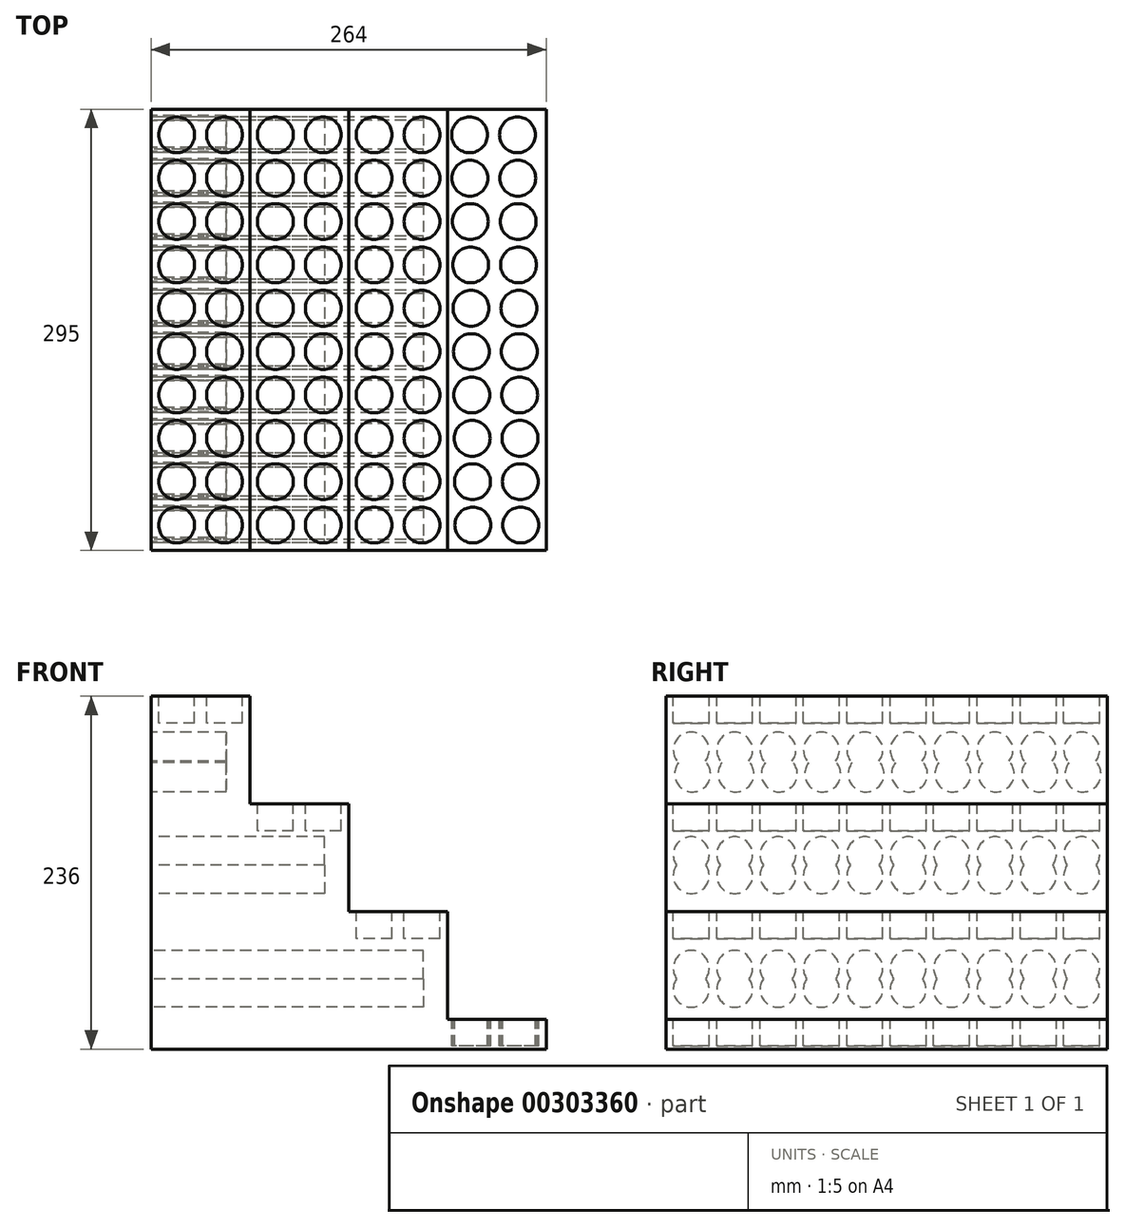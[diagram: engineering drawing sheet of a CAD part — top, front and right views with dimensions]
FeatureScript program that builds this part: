
annotation { "Feature Type Name" : "Feature", "Feature Type Description" : "" }
export const myFeature = defineFeature(function(context is Context, id is Id, definition is map)
    precondition{}
    {
        {
            var Q0;
            Q0=qCreatedBy(makeId("Front.planeOp"),FACE);
            var sketch = newSketch(context, id + "F0", { "sketchPlane" : qUnion([Q0])});
            skLineSegment(sketch, "E0", {"start": v(-130.71, -126.65) * mm, "end": v(133.29, -126.65) * mm});
            skLineSegment(sketch, "E1", {"start": v(133.29, -126.65) * mm, "end": v(133.29, -106.65) * mm});
            skLineSegment(sketch, "E2", {"start": v(133.29, -106.65) * mm, "end": v(67.29, -106.65) * mm});
            skLineSegment(sketch, "E3", {"start": v(67.29, -106.65) * mm, "end": v(67.29, -34.65) * mm});
            skLineSegment(sketch, "E4", {"start": v(67.29, -34.65) * mm, "end": v(1.29, -34.65) * mm});
            skLineSegment(sketch, "E5", {"start": v(1.29, -34.65) * mm, "end": v(1.29, 37.35) * mm});
            skLineSegment(sketch, "E6", {"start": v(1.29, 37.35) * mm, "end": v(-64.71, 37.35) * mm});
            skLineSegment(sketch, "E7", {"start": v(-64.71, 37.35) * mm, "end": v(-64.71, 109.35) * mm});
            skLineSegment(sketch, "E8", {"start": v(-64.71, 109.35) * mm, "end": v(-130.71, 109.35) * mm});
            skLineSegment(sketch, "E9", {"start": v(-130.71, 109.35) * mm, "end": v(-130.71, -126.65) * mm});
            skSolve(sketch);
        }
        {
            var Q0;
            Q0 = qSketchRegion(id + "F0", true);
            extrude(context, id + "F1", {"entities" : qUnion([Q0]), "depth" : 295 * mm});
        }
        {
            var Q0;
            Q0=makeQuery(id+"F1.opExtrude","SWEPT_FACE",FACE,{"disambiguationData":[OSD([sQuery(id+"F0.wireOp",EDGE,"E2")])]});
            var sketch = newSketch(context, id + "F2", { "sketchPlane" : qUnion([Q0])});
            skCircle(sketch, "E10", {"center": v(84.29, -278) * mm, "radius": 12 * mm});
            skCircle(sketch, "E11.0.1.0", {"center": v(84.04, -249) * mm, "radius": 12 * mm});
            skCircle(sketch, "E11.0.2.0", {"center": v(83.8, -220) * mm, "radius": 12 * mm});
            skCircle(sketch, "E11.0.3.0", {"center": v(83.55, -191) * mm, "radius": 12 * mm});
            skCircle(sketch, "E11.0.4.0", {"center": v(83.31, -162) * mm, "radius": 12 * mm});
            skCircle(sketch, "E11.0.5.0", {"center": v(83.07, -133) * mm, "radius": 12 * mm});
            skCircle(sketch, "E11.0.6.0", {"center": v(82.82, -104) * mm, "radius": 12 * mm});
            skCircle(sketch, "E11.0.7.0", {"center": v(82.58, -75) * mm, "radius": 12 * mm});
            skCircle(sketch, "E11.0.8.0", {"center": v(82.34, -46) * mm, "radius": 12 * mm});
            skCircle(sketch, "E11.0.9.0", {"center": v(82.1, -17) * mm, "radius": 12 * mm});
            skCircle(sketch, "E11.1.0.0", {"center": v(116.29, -278) * mm, "radius": 12 * mm});
            skCircle(sketch, "E11.1.1.0", {"center": v(116.04, -249) * mm, "radius": 12 * mm});
            skCircle(sketch, "E11.1.2.0", {"center": v(115.8, -220) * mm, "radius": 12 * mm});
            skCircle(sketch, "E11.1.3.0", {"center": v(115.55, -191) * mm, "radius": 12 * mm});
            skCircle(sketch, "E11.1.4.0", {"center": v(115.31, -162) * mm, "radius": 12 * mm});
            skCircle(sketch, "E11.1.5.0", {"center": v(115.07, -133) * mm, "radius": 12 * mm});
            skCircle(sketch, "E11.1.6.0", {"center": v(114.82, -104) * mm, "radius": 12 * mm});
            skCircle(sketch, "E11.1.7.0", {"center": v(114.58, -75) * mm, "radius": 12 * mm});
            skCircle(sketch, "E11.1.8.0", {"center": v(114.34, -46) * mm, "radius": 12 * mm});
            skCircle(sketch, "E11.1.9.0", {"center": v(114.1, -17) * mm, "radius": 12 * mm});
            skLineSegment(sketch, "E11.direction1", {"start": v(84.29, -278) * mm, "end": v(116.29, -278) * mm, "construction": true});
            skLineSegment(sketch, "E11.direction2", {"start": v(84.29, -278) * mm, "end": v(84.04, -249) * mm, "construction": true});
            skSolve(sketch);
        }
        {
            var Q0;
            Q0=makeQuery(id+"F2.imprint","IMPRINT",FACE,{"disambiguationData":[TD([[makeQuery(id+"F2.imprint","IMPRINT",EDGE,{"derivedFrom":sQuery(id+"F2.wireOp",EDGE,"E10")}),1.0]])]});
            var Q1;
            Q1=makeQuery(id+"F2.imprint","IMPRINT",FACE,{"disambiguationData":[TD([[makeQuery(id+"F2.imprint","IMPRINT",EDGE,{"derivedFrom":sQuery(id+"F2.wireOp",EDGE,"E11.0.1.0")}),1.0]])]});
            var Q2;
            Q2=makeQuery(id+"F2.imprint","IMPRINT",FACE,{"disambiguationData":[TD([[makeQuery(id+"F2.imprint","IMPRINT",EDGE,{"derivedFrom":sQuery(id+"F2.wireOp",EDGE,"E11.0.2.0")}),1.0]])]});
            var Q3;
            Q3=makeQuery(id+"F2.imprint","IMPRINT",FACE,{"disambiguationData":[TD([[makeQuery(id+"F2.imprint","IMPRINT",EDGE,{"derivedFrom":sQuery(id+"F2.wireOp",EDGE,"E11.0.3.0")}),1.0]])]});
            var Q4;
            Q4=makeQuery(id+"F2.imprint","IMPRINT",FACE,{"disambiguationData":[TD([[makeQuery(id+"F2.imprint","IMPRINT",EDGE,{"derivedFrom":sQuery(id+"F2.wireOp",EDGE,"E11.0.4.0")}),1.0]])]});
            var Q5;
            Q5=makeQuery(id+"F2.imprint","IMPRINT",FACE,{"disambiguationData":[TD([[makeQuery(id+"F2.imprint","IMPRINT",EDGE,{"derivedFrom":sQuery(id+"F2.wireOp",EDGE,"E11.0.5.0")}),1.0]])]});
            var Q6;
            Q6=makeQuery(id+"F2.imprint","IMPRINT",FACE,{"disambiguationData":[TD([[makeQuery(id+"F2.imprint","IMPRINT",EDGE,{"derivedFrom":sQuery(id+"F2.wireOp",EDGE,"E11.0.6.0")}),1.0]])]});
            var Q7;
            Q7=makeQuery(id+"F2.imprint","IMPRINT",FACE,{"disambiguationData":[TD([[makeQuery(id+"F2.imprint","IMPRINT",EDGE,{"derivedFrom":sQuery(id+"F2.wireOp",EDGE,"E11.0.7.0")}),1.0]])]});
            var Q8;
            Q8=makeQuery(id+"F2.imprint","IMPRINT",FACE,{"disambiguationData":[TD([[makeQuery(id+"F2.imprint","IMPRINT",EDGE,{"derivedFrom":sQuery(id+"F2.wireOp",EDGE,"E11.0.8.0")}),1.0]])]});
            var Q9;
            Q9=makeQuery(id+"F2.imprint","IMPRINT",FACE,{"disambiguationData":[TD([[makeQuery(id+"F2.imprint","IMPRINT",EDGE,{"derivedFrom":sQuery(id+"F2.wireOp",EDGE,"E11.0.9.0")}),1.0]])]});
            var Q10;
            Q10=makeQuery(id+"F2.imprint","IMPRINT",FACE,{"disambiguationData":[TD([[makeQuery(id+"F2.imprint","IMPRINT",EDGE,{"derivedFrom":sQuery(id+"F2.wireOp",EDGE,"E11.1.9.0")}),1.0]])]});
            var Q11;
            Q11=makeQuery(id+"F2.imprint","IMPRINT",FACE,{"disambiguationData":[TD([[makeQuery(id+"F2.imprint","IMPRINT",EDGE,{"derivedFrom":sQuery(id+"F2.wireOp",EDGE,"E11.1.8.0")}),1.0]])]});
            var Q12;
            Q12=makeQuery(id+"F2.imprint","IMPRINT",FACE,{"disambiguationData":[TD([[makeQuery(id+"F2.imprint","IMPRINT",EDGE,{"derivedFrom":sQuery(id+"F2.wireOp",EDGE,"E11.1.7.0")}),1.0]])]});
            var Q13;
            Q13=makeQuery(id+"F2.imprint","IMPRINT",FACE,{"disambiguationData":[TD([[makeQuery(id+"F2.imprint","IMPRINT",EDGE,{"derivedFrom":sQuery(id+"F2.wireOp",EDGE,"E11.1.6.0")}),1.0]])]});
            var Q14;
            Q14=makeQuery(id+"F2.imprint","IMPRINT",FACE,{"disambiguationData":[TD([[makeQuery(id+"F2.imprint","IMPRINT",EDGE,{"derivedFrom":sQuery(id+"F2.wireOp",EDGE,"E11.1.5.0")}),1.0]])]});
            var Q15;
            Q15=makeQuery(id+"F2.imprint","IMPRINT",FACE,{"disambiguationData":[TD([[makeQuery(id+"F2.imprint","IMPRINT",EDGE,{"derivedFrom":sQuery(id+"F2.wireOp",EDGE,"E11.1.4.0")}),1.0]])]});
            var Q16;
            Q16=makeQuery(id+"F2.imprint","IMPRINT",FACE,{"disambiguationData":[TD([[makeQuery(id+"F2.imprint","IMPRINT",EDGE,{"derivedFrom":sQuery(id+"F2.wireOp",EDGE,"E11.1.3.0")}),1.0]])]});
            var Q17;
            Q17=makeQuery(id+"F2.imprint","IMPRINT",FACE,{"disambiguationData":[TD([[makeQuery(id+"F2.imprint","IMPRINT",EDGE,{"derivedFrom":sQuery(id+"F2.wireOp",EDGE,"E11.1.2.0")}),1.0]])]});
            var Q18;
            Q18=makeQuery(id+"F2.imprint","IMPRINT",FACE,{"disambiguationData":[TD([[makeQuery(id+"F2.imprint","IMPRINT",EDGE,{"derivedFrom":sQuery(id+"F2.wireOp",EDGE,"E11.1.1.0")}),1.0]])]});
            var Q19;
            Q19=makeQuery(id+"F2.imprint","IMPRINT",FACE,{"disambiguationData":[TD([[makeQuery(id+"F2.imprint","IMPRINT",EDGE,{"derivedFrom":sQuery(id+"F2.wireOp",EDGE,"E11.1.0.0")}),1.0]])]});
            var Q20;
            Q20=sQuery(id+"F2.wireOp",EDGE,"E10");
            extrude(context, id + "F3", {"entities" : qUnion([Q0, Q1, Q2, Q3, Q4, Q5, Q6, Q7, Q8, Q9, Q10, Q11, Q12, Q13, Q14, Q15, Q16, Q17, Q18, Q19]), "operationType" : NewBodyOperationType.REMOVE, "surfaceEntities" : qUnion([Q20]), "oppositeDirection" : true, "depth" : 18 * mm});
        }
        {
            var Q0;
            Q0=makeQuery(id+"F1.opExtrude","SWEPT_FACE",FACE,{"disambiguationData":[OSD([sQuery(id+"F0.wireOp",EDGE,"E4")])]});
            var sketch = newSketch(context, id + "F4", { "sketchPlane" : qUnion([Q0])});
            skCircle(sketch, "E12", {"center": v(18.29, -278) * mm, "radius": 12 * mm});
            skCircle(sketch, "E13.0.1.0", {"center": v(18.29, -249) * mm, "radius": 12 * mm});
            skCircle(sketch, "E13.0.2.0", {"center": v(18.29, -220) * mm, "radius": 12 * mm});
            skCircle(sketch, "E13.0.3.0", {"center": v(18.29, -191) * mm, "radius": 12 * mm});
            skCircle(sketch, "E13.0.4.0", {"center": v(18.29, -162) * mm, "radius": 12 * mm});
            skCircle(sketch, "E13.0.5.0", {"center": v(18.29, -133) * mm, "radius": 12 * mm});
            skCircle(sketch, "E13.0.6.0", {"center": v(18.29, -104) * mm, "radius": 12 * mm});
            skCircle(sketch, "E13.0.7.0", {"center": v(18.29, -75) * mm, "radius": 12 * mm});
            skCircle(sketch, "E13.0.8.0", {"center": v(18.29, -46) * mm, "radius": 12 * mm});
            skCircle(sketch, "E13.0.9.0", {"center": v(18.29, -17) * mm, "radius": 12 * mm});
            skCircle(sketch, "E13.1.0.0", {"center": v(50.29, -278) * mm, "radius": 12 * mm});
            skCircle(sketch, "E13.1.1.0", {"center": v(50.29, -249) * mm, "radius": 12 * mm});
            skCircle(sketch, "E13.1.2.0", {"center": v(50.29, -220) * mm, "radius": 12 * mm});
            skCircle(sketch, "E13.1.3.0", {"center": v(50.29, -191) * mm, "radius": 12 * mm});
            skCircle(sketch, "E13.1.4.0", {"center": v(50.29, -162) * mm, "radius": 12 * mm});
            skCircle(sketch, "E13.1.5.0", {"center": v(50.29, -133) * mm, "radius": 12 * mm});
            skCircle(sketch, "E13.1.6.0", {"center": v(50.29, -104) * mm, "radius": 12 * mm});
            skCircle(sketch, "E13.1.7.0", {"center": v(50.29, -75) * mm, "radius": 12 * mm});
            skCircle(sketch, "E13.1.8.0", {"center": v(50.29, -46) * mm, "radius": 12 * mm});
            skCircle(sketch, "E13.1.9.0", {"center": v(50.29, -17) * mm, "radius": 12 * mm});
            skLineSegment(sketch, "E13.direction1", {"start": v(18.29, -278) * mm, "end": v(50.29, -278) * mm, "construction": true});
            skLineSegment(sketch, "E13.direction2", {"start": v(18.29, -278) * mm, "end": v(18.29, -249) * mm, "construction": true});
            skSolve(sketch);
        }
        {
            var Q0;
            Q0=makeQuery(id+"F4.imprint","IMPRINT",FACE,{"disambiguationData":[TD([[makeQuery(id+"F4.imprint","IMPRINT",EDGE,{"derivedFrom":sQuery(id+"F4.wireOp",EDGE,"E12")}),1.0]])]});
            var Q1;
            Q1=makeQuery(id+"F4.imprint","IMPRINT",FACE,{"disambiguationData":[TD([[makeQuery(id+"F4.imprint","IMPRINT",EDGE,{"derivedFrom":sQuery(id+"F4.wireOp",EDGE,"E13.0.1.0")}),1.0]])]});
            var Q2;
            Q2=makeQuery(id+"F4.imprint","IMPRINT",FACE,{"disambiguationData":[TD([[makeQuery(id+"F4.imprint","IMPRINT",EDGE,{"derivedFrom":sQuery(id+"F4.wireOp",EDGE,"E13.0.2.0")}),1.0]])]});
            var Q3;
            Q3=makeQuery(id+"F4.imprint","IMPRINT",FACE,{"disambiguationData":[TD([[makeQuery(id+"F4.imprint","IMPRINT",EDGE,{"derivedFrom":sQuery(id+"F4.wireOp",EDGE,"E13.0.3.0")}),1.0]])]});
            var Q4;
            Q4=makeQuery(id+"F4.imprint","IMPRINT",FACE,{"disambiguationData":[TD([[makeQuery(id+"F4.imprint","IMPRINT",EDGE,{"derivedFrom":sQuery(id+"F4.wireOp",EDGE,"E13.0.4.0")}),1.0]])]});
            var Q5;
            Q5=makeQuery(id+"F4.imprint","IMPRINT",FACE,{"disambiguationData":[TD([[makeQuery(id+"F4.imprint","IMPRINT",EDGE,{"derivedFrom":sQuery(id+"F4.wireOp",EDGE,"E13.0.5.0")}),1.0]])]});
            var Q6;
            Q6=makeQuery(id+"F4.imprint","IMPRINT",FACE,{"disambiguationData":[TD([[makeQuery(id+"F4.imprint","IMPRINT",EDGE,{"derivedFrom":sQuery(id+"F4.wireOp",EDGE,"E13.0.6.0")}),1.0]])]});
            var Q7;
            Q7=makeQuery(id+"F4.imprint","IMPRINT",FACE,{"disambiguationData":[TD([[makeQuery(id+"F4.imprint","IMPRINT",EDGE,{"derivedFrom":sQuery(id+"F4.wireOp",EDGE,"E13.0.7.0")}),1.0]])]});
            var Q8;
            Q8=makeQuery(id+"F4.imprint","IMPRINT",FACE,{"disambiguationData":[TD([[makeQuery(id+"F4.imprint","IMPRINT",EDGE,{"derivedFrom":sQuery(id+"F4.wireOp",EDGE,"E13.0.8.0")}),1.0]])]});
            var Q9;
            Q9=makeQuery(id+"F4.imprint","IMPRINT",FACE,{"disambiguationData":[TD([[makeQuery(id+"F4.imprint","IMPRINT",EDGE,{"derivedFrom":sQuery(id+"F4.wireOp",EDGE,"E13.0.9.0")}),1.0]])]});
            var Q10;
            Q10=makeQuery(id+"F4.imprint","IMPRINT",FACE,{"disambiguationData":[TD([[makeQuery(id+"F4.imprint","IMPRINT",EDGE,{"derivedFrom":sQuery(id+"F4.wireOp",EDGE,"E13.1.9.0")}),1.0]])]});
            var Q11;
            Q11=makeQuery(id+"F4.imprint","IMPRINT",FACE,{"disambiguationData":[TD([[makeQuery(id+"F4.imprint","IMPRINT",EDGE,{"derivedFrom":sQuery(id+"F4.wireOp",EDGE,"E13.1.8.0")}),1.0]])]});
            var Q12;
            Q12=makeQuery(id+"F4.imprint","IMPRINT",FACE,{"disambiguationData":[TD([[makeQuery(id+"F4.imprint","IMPRINT",EDGE,{"derivedFrom":sQuery(id+"F4.wireOp",EDGE,"E13.1.7.0")}),1.0]])]});
            var Q13;
            Q13=makeQuery(id+"F4.imprint","IMPRINT",FACE,{"disambiguationData":[TD([[makeQuery(id+"F4.imprint","IMPRINT",EDGE,{"derivedFrom":sQuery(id+"F4.wireOp",EDGE,"E13.1.6.0")}),1.0]])]});
            var Q14;
            Q14=makeQuery(id+"F4.imprint","IMPRINT",FACE,{"disambiguationData":[TD([[makeQuery(id+"F4.imprint","IMPRINT",EDGE,{"derivedFrom":sQuery(id+"F4.wireOp",EDGE,"E13.1.5.0")}),1.0]])]});
            var Q15;
            Q15=makeQuery(id+"F4.imprint","IMPRINT",FACE,{"disambiguationData":[TD([[makeQuery(id+"F4.imprint","IMPRINT",EDGE,{"derivedFrom":sQuery(id+"F4.wireOp",EDGE,"E13.1.4.0")}),1.0]])]});
            var Q16;
            Q16=makeQuery(id+"F4.imprint","IMPRINT",FACE,{"disambiguationData":[TD([[makeQuery(id+"F4.imprint","IMPRINT",EDGE,{"derivedFrom":sQuery(id+"F4.wireOp",EDGE,"E13.1.3.0")}),1.0]])]});
            var Q17;
            Q17=makeQuery(id+"F4.imprint","IMPRINT",FACE,{"disambiguationData":[TD([[makeQuery(id+"F4.imprint","IMPRINT",EDGE,{"derivedFrom":sQuery(id+"F4.wireOp",EDGE,"E13.1.2.0")}),1.0]])]});
            var Q18;
            Q18=makeQuery(id+"F4.imprint","IMPRINT",FACE,{"disambiguationData":[TD([[makeQuery(id+"F4.imprint","IMPRINT",EDGE,{"derivedFrom":sQuery(id+"F4.wireOp",EDGE,"E13.1.1.0")}),1.0]])]});
            var Q19;
            Q19=makeQuery(id+"F4.imprint","IMPRINT",FACE,{"disambiguationData":[TD([[makeQuery(id+"F4.imprint","IMPRINT",EDGE,{"derivedFrom":sQuery(id+"F4.wireOp",EDGE,"E13.1.0.0")}),1.0]])]});
            var Q20;
            Q20=sQuery(id+"F4.wireOp",EDGE,"E12");
            extrude(context, id + "F5", {"entities" : qUnion([Q0, Q1, Q2, Q3, Q4, Q5, Q6, Q7, Q8, Q9, Q10, Q11, Q12, Q13, Q14, Q15, Q16, Q17, Q18, Q19]), "operationType" : NewBodyOperationType.REMOVE, "surfaceEntities" : qUnion([Q20]), "oppositeDirection" : true, "depth" : 18 * mm});
        }
        {
            var Q0;
            Q0=makeQuery(id+"F1.opExtrude","SWEPT_FACE",FACE,{"disambiguationData":[OSD([sQuery(id+"F0.wireOp",EDGE,"E6")])]});
            var sketch = newSketch(context, id + "F6", { "sketchPlane" : qUnion([Q0])});
            skCircle(sketch, "E14", {"center": v(-47.71, -278) * mm, "radius": 12 * mm});
            skCircle(sketch, "E15.0.1.0", {"center": v(-47.71, -249) * mm, "radius": 12 * mm});
            skCircle(sketch, "E15.0.2.0", {"center": v(-47.71, -220) * mm, "radius": 12 * mm});
            skCircle(sketch, "E15.0.3.0", {"center": v(-47.71, -191) * mm, "radius": 12 * mm});
            skCircle(sketch, "E15.0.4.0", {"center": v(-47.71, -162) * mm, "radius": 12 * mm});
            skCircle(sketch, "E15.0.5.0", {"center": v(-47.71, -133) * mm, "radius": 12 * mm});
            skCircle(sketch, "E15.0.6.0", {"center": v(-47.71, -104) * mm, "radius": 12 * mm});
            skCircle(sketch, "E15.0.7.0", {"center": v(-47.71, -75) * mm, "radius": 12 * mm});
            skCircle(sketch, "E15.0.8.0", {"center": v(-47.71, -46) * mm, "radius": 12 * mm});
            skCircle(sketch, "E15.0.9.0", {"center": v(-47.71, -17) * mm, "radius": 12 * mm});
            skCircle(sketch, "E15.1.0.0", {"center": v(-15.71, -278) * mm, "radius": 12 * mm});
            skCircle(sketch, "E15.1.1.0", {"center": v(-15.71, -249) * mm, "radius": 12 * mm});
            skCircle(sketch, "E15.1.2.0", {"center": v(-15.71, -220) * mm, "radius": 12 * mm});
            skCircle(sketch, "E15.1.3.0", {"center": v(-15.71, -191) * mm, "radius": 12 * mm});
            skCircle(sketch, "E15.1.4.0", {"center": v(-15.71, -162) * mm, "radius": 12 * mm});
            skCircle(sketch, "E15.1.5.0", {"center": v(-15.71, -133) * mm, "radius": 12 * mm});
            skCircle(sketch, "E15.1.6.0", {"center": v(-15.71, -104) * mm, "radius": 12 * mm});
            skCircle(sketch, "E15.1.7.0", {"center": v(-15.71, -75) * mm, "radius": 12 * mm});
            skCircle(sketch, "E15.1.8.0", {"center": v(-15.71, -46) * mm, "radius": 12 * mm});
            skCircle(sketch, "E15.1.9.0", {"center": v(-15.71, -17) * mm, "radius": 12 * mm});
            skLineSegment(sketch, "E15.direction1", {"start": v(-47.71, -278) * mm, "end": v(-15.71, -278) * mm, "construction": true});
            skLineSegment(sketch, "E15.direction2", {"start": v(-47.71, -278) * mm, "end": v(-47.71, -249) * mm, "construction": true});
            skSolve(sketch);
        }
        {
            var Q0;
            Q0=makeQuery(id+"F6.imprint","IMPRINT",FACE,{"disambiguationData":[TD([[makeQuery(id+"F6.imprint","IMPRINT",EDGE,{"derivedFrom":sQuery(id+"F6.wireOp",EDGE,"E14")}),1.0]])]});
            var Q1;
            Q1=makeQuery(id+"F6.imprint","IMPRINT",FACE,{"disambiguationData":[TD([[makeQuery(id+"F6.imprint","IMPRINT",EDGE,{"derivedFrom":sQuery(id+"F6.wireOp",EDGE,"E15.0.1.0")}),1.0]])]});
            var Q2;
            Q2=makeQuery(id+"F6.imprint","IMPRINT",FACE,{"disambiguationData":[TD([[makeQuery(id+"F6.imprint","IMPRINT",EDGE,{"derivedFrom":sQuery(id+"F6.wireOp",EDGE,"E15.0.2.0")}),1.0]])]});
            var Q3;
            Q3=makeQuery(id+"F6.imprint","IMPRINT",FACE,{"disambiguationData":[TD([[makeQuery(id+"F6.imprint","IMPRINT",EDGE,{"derivedFrom":sQuery(id+"F6.wireOp",EDGE,"E15.0.3.0")}),1.0]])]});
            var Q4;
            Q4=makeQuery(id+"F6.imprint","IMPRINT",FACE,{"disambiguationData":[TD([[makeQuery(id+"F6.imprint","IMPRINT",EDGE,{"derivedFrom":sQuery(id+"F6.wireOp",EDGE,"E15.0.4.0")}),1.0]])]});
            var Q5;
            Q5=makeQuery(id+"F6.imprint","IMPRINT",FACE,{"disambiguationData":[TD([[makeQuery(id+"F6.imprint","IMPRINT",EDGE,{"derivedFrom":sQuery(id+"F6.wireOp",EDGE,"E15.0.5.0")}),1.0]])]});
            var Q6;
            Q6=makeQuery(id+"F6.imprint","IMPRINT",FACE,{"disambiguationData":[TD([[makeQuery(id+"F6.imprint","IMPRINT",EDGE,{"derivedFrom":sQuery(id+"F6.wireOp",EDGE,"E15.0.6.0")}),1.0]])]});
            var Q7;
            Q7=makeQuery(id+"F6.imprint","IMPRINT",FACE,{"disambiguationData":[TD([[makeQuery(id+"F6.imprint","IMPRINT",EDGE,{"derivedFrom":sQuery(id+"F6.wireOp",EDGE,"E15.0.7.0")}),1.0]])]});
            var Q8;
            Q8=makeQuery(id+"F6.imprint","IMPRINT",FACE,{"disambiguationData":[TD([[makeQuery(id+"F6.imprint","IMPRINT",EDGE,{"derivedFrom":sQuery(id+"F6.wireOp",EDGE,"E15.0.8.0")}),1.0]])]});
            var Q9;
            Q9=makeQuery(id+"F6.imprint","IMPRINT",FACE,{"disambiguationData":[TD([[makeQuery(id+"F6.imprint","IMPRINT",EDGE,{"derivedFrom":sQuery(id+"F6.wireOp",EDGE,"E15.0.9.0")}),1.0]])]});
            var Q10;
            Q10=makeQuery(id+"F6.imprint","IMPRINT",FACE,{"disambiguationData":[TD([[makeQuery(id+"F6.imprint","IMPRINT",EDGE,{"derivedFrom":sQuery(id+"F6.wireOp",EDGE,"E15.1.9.0")}),1.0]])]});
            var Q11;
            Q11=makeQuery(id+"F6.imprint","IMPRINT",FACE,{"disambiguationData":[TD([[makeQuery(id+"F6.imprint","IMPRINT",EDGE,{"derivedFrom":sQuery(id+"F6.wireOp",EDGE,"E15.1.8.0")}),1.0]])]});
            var Q12;
            Q12=makeQuery(id+"F6.imprint","IMPRINT",FACE,{"disambiguationData":[TD([[makeQuery(id+"F6.imprint","IMPRINT",EDGE,{"derivedFrom":sQuery(id+"F6.wireOp",EDGE,"E15.1.7.0")}),1.0]])]});
            var Q13;
            Q13=makeQuery(id+"F6.imprint","IMPRINT",FACE,{"disambiguationData":[TD([[makeQuery(id+"F6.imprint","IMPRINT",EDGE,{"derivedFrom":sQuery(id+"F6.wireOp",EDGE,"E15.1.6.0")}),1.0]])]});
            var Q14;
            Q14=makeQuery(id+"F6.imprint","IMPRINT",FACE,{"disambiguationData":[TD([[makeQuery(id+"F6.imprint","IMPRINT",EDGE,{"derivedFrom":sQuery(id+"F6.wireOp",EDGE,"E15.1.5.0")}),1.0]])]});
            var Q15;
            Q15=makeQuery(id+"F6.imprint","IMPRINT",FACE,{"disambiguationData":[TD([[makeQuery(id+"F6.imprint","IMPRINT",EDGE,{"derivedFrom":sQuery(id+"F6.wireOp",EDGE,"E15.1.4.0")}),1.0]])]});
            var Q16;
            Q16=makeQuery(id+"F6.imprint","IMPRINT",FACE,{"disambiguationData":[TD([[makeQuery(id+"F6.imprint","IMPRINT",EDGE,{"derivedFrom":sQuery(id+"F6.wireOp",EDGE,"E15.1.3.0")}),1.0]])]});
            var Q17;
            Q17=makeQuery(id+"F6.imprint","IMPRINT",FACE,{"disambiguationData":[TD([[makeQuery(id+"F6.imprint","IMPRINT",EDGE,{"derivedFrom":sQuery(id+"F6.wireOp",EDGE,"E15.1.2.0")}),1.0]])]});
            var Q18;
            Q18=makeQuery(id+"F6.imprint","IMPRINT",FACE,{"disambiguationData":[TD([[makeQuery(id+"F6.imprint","IMPRINT",EDGE,{"derivedFrom":sQuery(id+"F6.wireOp",EDGE,"E15.1.1.0")}),1.0]])]});
            var Q19;
            Q19=makeQuery(id+"F6.imprint","IMPRINT",FACE,{"disambiguationData":[TD([[makeQuery(id+"F6.imprint","IMPRINT",EDGE,{"derivedFrom":sQuery(id+"F6.wireOp",EDGE,"E15.1.0.0")}),1.0]])]});
            var Q20;
            Q20=makeQuery(id+"F6.imprint","IMPRINT",EDGE,{"derivedFrom":sQuery(id+"F6.wireOp",EDGE,"E14")});
            extrude(context, id + "F7", {"entities" : qUnion([Q0, Q1, Q2, Q3, Q4, Q5, Q6, Q7, Q8, Q9, Q10, Q11, Q12, Q13, Q14, Q15, Q16, Q17, Q18, Q19]), "operationType" : NewBodyOperationType.REMOVE, "surfaceEntities" : qUnion([Q20]), "oppositeDirection" : true, "depth" : 18 * mm});
        }
        {
            var Q0;
            Q0=makeQuery(id+"F1.opExtrude","SWEPT_FACE",FACE,{"disambiguationData":[OSD([sQuery(id+"F0.wireOp",EDGE,"E8")])]});
            var sketch = newSketch(context, id + "F8", { "sketchPlane" : qUnion([Q0])});
            skCircle(sketch, "E16", {"center": v(-113.71, -278) * mm, "radius": 12 * mm});
            skCircle(sketch, "E17.0.1.0", {"center": v(-113.71, -249) * mm, "radius": 12 * mm});
            skCircle(sketch, "E17.0.2.0", {"center": v(-113.71, -220) * mm, "radius": 12 * mm});
            skCircle(sketch, "E17.0.3.0", {"center": v(-113.71, -191) * mm, "radius": 12 * mm});
            skCircle(sketch, "E17.0.4.0", {"center": v(-113.71, -162) * mm, "radius": 12 * mm});
            skCircle(sketch, "E17.0.5.0", {"center": v(-113.71, -133) * mm, "radius": 12 * mm});
            skCircle(sketch, "E17.0.6.0", {"center": v(-113.71, -104) * mm, "radius": 12 * mm});
            skCircle(sketch, "E17.0.7.0", {"center": v(-113.71, -75) * mm, "radius": 12 * mm});
            skCircle(sketch, "E17.0.8.0", {"center": v(-113.71, -46) * mm, "radius": 12 * mm});
            skCircle(sketch, "E17.0.9.0", {"center": v(-113.71, -17) * mm, "radius": 12 * mm});
            skCircle(sketch, "E17.1.0.0", {"center": v(-81.71, -278) * mm, "radius": 12 * mm});
            skCircle(sketch, "E17.1.1.0", {"center": v(-81.71, -249) * mm, "radius": 12 * mm});
            skCircle(sketch, "E17.1.2.0", {"center": v(-81.71, -220) * mm, "radius": 12 * mm});
            skCircle(sketch, "E17.1.3.0", {"center": v(-81.71, -191) * mm, "radius": 12 * mm});
            skCircle(sketch, "E17.1.4.0", {"center": v(-81.71, -162) * mm, "radius": 12 * mm});
            skCircle(sketch, "E17.1.5.0", {"center": v(-81.71, -133) * mm, "radius": 12 * mm});
            skCircle(sketch, "E17.1.6.0", {"center": v(-81.71, -104) * mm, "radius": 12 * mm});
            skCircle(sketch, "E17.1.7.0", {"center": v(-81.71, -75) * mm, "radius": 12 * mm});
            skCircle(sketch, "E17.1.8.0", {"center": v(-81.71, -46) * mm, "radius": 12 * mm});
            skCircle(sketch, "E17.1.9.0", {"center": v(-81.71, -17) * mm, "radius": 12 * mm});
            skLineSegment(sketch, "E17.direction1", {"start": v(-113.71, -278) * mm, "end": v(-81.71, -278) * mm, "construction": true});
            skLineSegment(sketch, "E17.direction2", {"start": v(-113.71, -278) * mm, "end": v(-113.71, -249) * mm, "construction": true});
            skSolve(sketch);
        }
        {
            var Q0;
            Q0=makeQuery(id+"F8.imprint","IMPRINT",FACE,{"disambiguationData":[TD([[makeQuery(id+"F8.imprint","IMPRINT",EDGE,{"derivedFrom":sQuery(id+"F8.wireOp",EDGE,"E16")}),1.0]])]});
            var Q1;
            Q1=makeQuery(id+"F8.imprint","IMPRINT",FACE,{"disambiguationData":[TD([[makeQuery(id+"F8.imprint","IMPRINT",EDGE,{"derivedFrom":sQuery(id+"F8.wireOp",EDGE,"E17.0.1.0")}),1.0]])]});
            var Q2;
            Q2=makeQuery(id+"F8.imprint","IMPRINT",FACE,{"disambiguationData":[TD([[makeQuery(id+"F8.imprint","IMPRINT",EDGE,{"derivedFrom":sQuery(id+"F8.wireOp",EDGE,"E17.0.2.0")}),1.0]])]});
            var Q3;
            Q3=makeQuery(id+"F8.imprint","IMPRINT",FACE,{"disambiguationData":[TD([[makeQuery(id+"F8.imprint","IMPRINT",EDGE,{"derivedFrom":sQuery(id+"F8.wireOp",EDGE,"E17.0.3.0")}),1.0]])]});
            var Q4;
            Q4=makeQuery(id+"F8.imprint","IMPRINT",FACE,{"disambiguationData":[TD([[makeQuery(id+"F8.imprint","IMPRINT",EDGE,{"derivedFrom":sQuery(id+"F8.wireOp",EDGE,"E17.0.4.0")}),1.0]])]});
            var Q5;
            Q5=makeQuery(id+"F8.imprint","IMPRINT",FACE,{"disambiguationData":[TD([[makeQuery(id+"F8.imprint","IMPRINT",EDGE,{"derivedFrom":sQuery(id+"F8.wireOp",EDGE,"E17.0.5.0")}),1.0]])]});
            var Q6;
            Q6=makeQuery(id+"F8.imprint","IMPRINT",FACE,{"disambiguationData":[TD([[makeQuery(id+"F8.imprint","IMPRINT",EDGE,{"derivedFrom":sQuery(id+"F8.wireOp",EDGE,"E17.0.6.0")}),1.0]])]});
            var Q7;
            Q7=makeQuery(id+"F8.imprint","IMPRINT",FACE,{"disambiguationData":[TD([[makeQuery(id+"F8.imprint","IMPRINT",EDGE,{"derivedFrom":sQuery(id+"F8.wireOp",EDGE,"E17.0.7.0")}),1.0]])]});
            var Q8;
            Q8=makeQuery(id+"F8.imprint","IMPRINT",FACE,{"disambiguationData":[TD([[makeQuery(id+"F8.imprint","IMPRINT",EDGE,{"derivedFrom":sQuery(id+"F8.wireOp",EDGE,"E17.0.8.0")}),1.0]])]});
            var Q9;
            Q9=makeQuery(id+"F8.imprint","IMPRINT",FACE,{"disambiguationData":[TD([[makeQuery(id+"F8.imprint","IMPRINT",EDGE,{"derivedFrom":sQuery(id+"F8.wireOp",EDGE,"E17.0.9.0")}),1.0]])]});
            var Q10;
            Q10=makeQuery(id+"F8.imprint","IMPRINT",FACE,{"disambiguationData":[TD([[makeQuery(id+"F8.imprint","IMPRINT",EDGE,{"derivedFrom":sQuery(id+"F8.wireOp",EDGE,"E17.1.9.0")}),1.0]])]});
            var Q11;
            Q11=makeQuery(id+"F8.imprint","IMPRINT",FACE,{"disambiguationData":[TD([[makeQuery(id+"F8.imprint","IMPRINT",EDGE,{"derivedFrom":sQuery(id+"F8.wireOp",EDGE,"E17.1.8.0")}),1.0]])]});
            var Q12;
            Q12=makeQuery(id+"F8.imprint","IMPRINT",FACE,{"disambiguationData":[TD([[makeQuery(id+"F8.imprint","IMPRINT",EDGE,{"derivedFrom":sQuery(id+"F8.wireOp",EDGE,"E17.1.7.0")}),1.0]])]});
            var Q13;
            Q13=makeQuery(id+"F8.imprint","IMPRINT",FACE,{"disambiguationData":[TD([[makeQuery(id+"F8.imprint","IMPRINT",EDGE,{"derivedFrom":sQuery(id+"F8.wireOp",EDGE,"E17.1.6.0")}),1.0]])]});
            var Q14;
            Q14=makeQuery(id+"F8.imprint","IMPRINT",FACE,{"disambiguationData":[TD([[makeQuery(id+"F8.imprint","IMPRINT",EDGE,{"derivedFrom":sQuery(id+"F8.wireOp",EDGE,"E17.1.5.0")}),1.0]])]});
            var Q15;
            Q15=makeQuery(id+"F8.imprint","IMPRINT",FACE,{"disambiguationData":[TD([[makeQuery(id+"F8.imprint","IMPRINT",EDGE,{"derivedFrom":sQuery(id+"F8.wireOp",EDGE,"E17.1.4.0")}),1.0]])]});
            var Q16;
            Q16=makeQuery(id+"F8.imprint","IMPRINT",FACE,{"disambiguationData":[TD([[makeQuery(id+"F8.imprint","IMPRINT",EDGE,{"derivedFrom":sQuery(id+"F8.wireOp",EDGE,"E17.1.3.0")}),1.0]])]});
            var Q17;
            Q17=makeQuery(id+"F8.imprint","IMPRINT",FACE,{"disambiguationData":[TD([[makeQuery(id+"F8.imprint","IMPRINT",EDGE,{"derivedFrom":sQuery(id+"F8.wireOp",EDGE,"E17.1.2.0")}),1.0]])]});
            var Q18;
            Q18=makeQuery(id+"F8.imprint","IMPRINT",FACE,{"disambiguationData":[TD([[makeQuery(id+"F8.imprint","IMPRINT",EDGE,{"derivedFrom":sQuery(id+"F8.wireOp",EDGE,"E17.1.1.0")}),1.0]])]});
            var Q19;
            Q19=makeQuery(id+"F8.imprint","IMPRINT",FACE,{"disambiguationData":[TD([[makeQuery(id+"F8.imprint","IMPRINT",EDGE,{"derivedFrom":sQuery(id+"F8.wireOp",EDGE,"E17.1.0.0")}),1.0]])]});
            var Q20;
            Q20 = qSketchRegion(id + "F10", true);
            var Q21;
            Q21=sQuery(id+"F8.wireOp",EDGE,"E16");
            extrude(context, id + "F9", {"entities" : qUnion([Q0, Q1, Q2, Q3, Q4, Q5, Q6, Q7, Q8, Q9, Q10, Q11, Q12, Q13, Q14, Q15, Q16, Q17, Q18, Q19, Q20]), "operationType" : NewBodyOperationType.REMOVE, "surfaceEntities" : qUnion([Q21]), "oppositeDirection" : true, "depth" : 18 * mm});
        }
        {
            var Q0;
            Q0=makeQuery(id+"F1.opExtrude","SWEPT_FACE",FACE,{"disambiguationData":[OSD([sQuery(id+"F0.wireOp",EDGE,"E9")])]});
            var sketch = newSketch(context, id + "F10", { "sketchPlane" : qUnion([Q0])});
            skCircle(sketch, "E18", {"center": v(17, -86.65) * mm, "radius": 12 * mm});
            skCircle(sketch, "E19.1.0.0", {"center": v(46, -86.65) * mm, "radius": 12 * mm});
            skCircle(sketch, "E19.2.0.0", {"center": v(75, -86.65) * mm, "radius": 12 * mm});
            skCircle(sketch, "E19.3.0.0", {"center": v(104, -86.65) * mm, "radius": 12 * mm});
            skCircle(sketch, "E19.4.0.0", {"center": v(133, -86.65) * mm, "radius": 12 * mm});
            skCircle(sketch, "E19.5.0.0", {"center": v(162, -86.65) * mm, "radius": 12 * mm});
            skCircle(sketch, "E19.6.0.0", {"center": v(191, -86.65) * mm, "radius": 12 * mm});
            skCircle(sketch, "E19.7.0.0", {"center": v(220, -86.65) * mm, "radius": 12 * mm});
            skCircle(sketch, "E19.8.0.0", {"center": v(249, -86.65) * mm, "radius": 12 * mm});
            skCircle(sketch, "E19.9.0.0", {"center": v(278, -86.65) * mm, "radius": 12 * mm});
            skLineSegment(sketch, "E19.direction1", {"start": v(17, -86.65) * mm, "end": v(46, -86.65) * mm, "construction": true});
            skLineSegment(sketch, "E20.0", {"start": v(295, -126.65) * mm, "end": v(0, -126.65) * mm});
            skPoint(sketch, "E21.0", {"position": v(0, 0) * mm});
            skLineSegment(sketch, "E22.0.1", {"start": v(0, -126.65) * mm, "end": v(295, -126.65) * mm});
            skCircle(sketch, "E23", {"center": v(17, -72.65) * mm, "radius": 12 * mm});
            skCircle(sketch, "E24.1.0.0", {"center": v(46, -72.65) * mm, "radius": 12 * mm});
            skCircle(sketch, "E24.2.0.0", {"center": v(75, -72.65) * mm, "radius": 12 * mm});
            skCircle(sketch, "E24.3.0.0", {"center": v(104, -72.65) * mm, "radius": 12 * mm});
            skCircle(sketch, "E24.4.0.0", {"center": v(133, -72.65) * mm, "radius": 12 * mm});
            skCircle(sketch, "E24.5.0.0", {"center": v(162, -72.65) * mm, "radius": 12 * mm});
            skCircle(sketch, "E24.6.0.0", {"center": v(191, -72.65) * mm, "radius": 12 * mm});
            skCircle(sketch, "E24.7.0.0", {"center": v(220, -72.65) * mm, "radius": 12 * mm});
            skCircle(sketch, "E24.8.0.0", {"center": v(249, -72.65) * mm, "radius": 12 * mm});
            skCircle(sketch, "E24.9.0.0", {"center": v(278, -72.65) * mm, "radius": 12 * mm});
            skLineSegment(sketch, "E24.direction1", {"start": v(17, -72.65) * mm, "end": v(46, -72.65) * mm, "construction": true});
            skSolve(sketch);
        }
        {
            var Q0;
            Q0=makeQuery(id+"F10.imprint","IMPRINT",FACE,{"disambiguationData":[TD([[makeQuery(id+"F10.imprint","IMPRINT",EDGE,{"derivedFrom":sQuery(id+"F10.wireOp",EDGE,"E18")}),1.0]])]});
            var Q1;
            Q1=makeQuery(id+"F10.imprint","IMPRINT",FACE,{"disambiguationData":[TD([[makeQuery(id+"F10.imprint","IMPRINT",EDGE,{"derivedFrom":sQuery(id+"F10.wireOp",EDGE,"E19.1.0.0")}),1.0]])]});
            var Q2;
            Q2=makeQuery(id+"F10.imprint","IMPRINT",FACE,{"disambiguationData":[TD([[makeQuery(id+"F10.imprint","IMPRINT",EDGE,{"derivedFrom":sQuery(id+"F10.wireOp",EDGE,"E19.2.0.0")}),1.0]])]});
            var Q3;
            Q3=makeQuery(id+"F10.imprint","IMPRINT",FACE,{"disambiguationData":[TD([[makeQuery(id+"F10.imprint","IMPRINT",EDGE,{"derivedFrom":sQuery(id+"F10.wireOp",EDGE,"E19.3.0.0")}),1.0]])]});
            var Q4;
            Q4=makeQuery(id+"F10.imprint","IMPRINT",FACE,{"disambiguationData":[TD([[makeQuery(id+"F10.imprint","IMPRINT",EDGE,{"derivedFrom":sQuery(id+"F10.wireOp",EDGE,"E19.4.0.0")}),1.0]])]});
            var Q5;
            Q5=makeQuery(id+"F10.imprint","IMPRINT",FACE,{"disambiguationData":[TD([[makeQuery(id+"F10.imprint","IMPRINT",EDGE,{"derivedFrom":sQuery(id+"F10.wireOp",EDGE,"E19.5.0.0")}),1.0]])]});
            var Q6;
            Q6=makeQuery(id+"F10.imprint","IMPRINT",FACE,{"disambiguationData":[TD([[makeQuery(id+"F10.imprint","IMPRINT",EDGE,{"derivedFrom":sQuery(id+"F10.wireOp",EDGE,"E19.6.0.0")}),1.0]])]});
            var Q7;
            Q7=makeQuery(id+"F10.imprint","IMPRINT",FACE,{"disambiguationData":[TD([[makeQuery(id+"F10.imprint","IMPRINT",EDGE,{"derivedFrom":sQuery(id+"F10.wireOp",EDGE,"E19.7.0.0")}),1.0]])]});
            var Q8;
            Q8=makeQuery(id+"F10.imprint","IMPRINT",FACE,{"disambiguationData":[TD([[makeQuery(id+"F10.imprint","IMPRINT",EDGE,{"derivedFrom":sQuery(id+"F10.wireOp",EDGE,"E19.8.0.0")}),1.0]])]});
            var Q9;
            Q9=makeQuery(id+"F10.imprint","IMPRINT",FACE,{"disambiguationData":[TD([[makeQuery(id+"F10.imprint","IMPRINT",EDGE,{"derivedFrom":sQuery(id+"F10.wireOp",EDGE,"E19.9.0.0")}),1.0]])]});
            extrude(context, id + "F11", {"entities" : qUnion([Q0, Q1, Q2, Q3, Q4, Q5, Q6, Q7, Q8, Q9]), "operationType" : NewBodyOperationType.REMOVE, "oppositeDirection" : true, "depth" : 180 * mm});
        }
        {
            var Q0;
            Q0=makeQuery(id+"F1.opExtrude","SWEPT_FACE",FACE,{"disambiguationData":[OSD([sQuery(id+"F0.wireOp",EDGE,"E9")])]});
            var sketch = newSketch(context, id + "F12", { "sketchPlane" : qUnion([Q0])});
            skCircle(sketch, "E25", {"center": v(17, -10.65) * mm, "radius": 12 * mm});
            skCircle(sketch, "E26.1.0.0", {"center": v(46, -10.65) * mm, "radius": 12 * mm});
            skCircle(sketch, "E26.2.0.0", {"center": v(75, -10.65) * mm, "radius": 12 * mm});
            skCircle(sketch, "E26.3.0.0", {"center": v(104, -10.65) * mm, "radius": 12 * mm});
            skCircle(sketch, "E26.4.0.0", {"center": v(133, -10.65) * mm, "radius": 12 * mm});
            skCircle(sketch, "E26.5.0.0", {"center": v(162, -10.65) * mm, "radius": 12 * mm});
            skCircle(sketch, "E26.6.0.0", {"center": v(191, -10.65) * mm, "radius": 12 * mm});
            skCircle(sketch, "E26.7.0.0", {"center": v(220, -10.65) * mm, "radius": 12 * mm});
            skCircle(sketch, "E26.8.0.0", {"center": v(249, -10.65) * mm, "radius": 12 * mm});
            skCircle(sketch, "E26.9.0.0", {"center": v(278, -10.65) * mm, "radius": 12 * mm});
            skLineSegment(sketch, "E26.direction1", {"start": v(17, -10.65) * mm, "end": v(46, -10.65) * mm, "construction": true});
            skCircle(sketch, "E27", {"center": v(17, 3.35) * mm, "radius": 12 * mm});
            skCircle(sketch, "E28.1.0.0", {"center": v(46, 3.35) * mm, "radius": 12 * mm});
            skCircle(sketch, "E28.2.0.0", {"center": v(75, 3.35) * mm, "radius": 12 * mm});
            skCircle(sketch, "E28.3.0.0", {"center": v(104, 3.35) * mm, "radius": 12 * mm});
            skCircle(sketch, "E28.4.0.0", {"center": v(133, 3.35) * mm, "radius": 12 * mm});
            skCircle(sketch, "E28.5.0.0", {"center": v(162, 3.35) * mm, "radius": 12 * mm});
            skCircle(sketch, "E28.6.0.0", {"center": v(191, 3.35) * mm, "radius": 12 * mm});
            skCircle(sketch, "E28.7.0.0", {"center": v(220, 3.35) * mm, "radius": 12 * mm});
            skCircle(sketch, "E28.8.0.0", {"center": v(249, 3.35) * mm, "radius": 12 * mm});
            skCircle(sketch, "E28.9.0.0", {"center": v(278, 3.35) * mm, "radius": 12 * mm});
            skLineSegment(sketch, "E28.direction1", {"start": v(17, 3.35) * mm, "end": v(46, 3.35) * mm, "construction": true});
            skSolve(sketch);
        }
        {
            var Q0;
            Q0=makeQuery(id+"F12.imprint","IMPRINT",FACE,{"disambiguationData":[TD([[makeQuery(id+"F12.imprint","IMPRINT",EDGE,{"derivedFrom":sQuery(id+"F12.wireOp",EDGE,"E25")}),1.0]])]});
            var Q1;
            Q1=makeQuery(id+"F12.imprint","IMPRINT",FACE,{"disambiguationData":[TD([[makeQuery(id+"F12.imprint","IMPRINT",EDGE,{"derivedFrom":sQuery(id+"F12.wireOp",EDGE,"E26.1.0.0")}),1.0]])]});
            var Q2;
            Q2=makeQuery(id+"F12.imprint","IMPRINT",FACE,{"disambiguationData":[TD([[makeQuery(id+"F12.imprint","IMPRINT",EDGE,{"derivedFrom":sQuery(id+"F12.wireOp",EDGE,"E26.2.0.0")}),1.0]])]});
            var Q3;
            Q3=makeQuery(id+"F12.imprint","IMPRINT",FACE,{"disambiguationData":[TD([[makeQuery(id+"F12.imprint","IMPRINT",EDGE,{"derivedFrom":sQuery(id+"F12.wireOp",EDGE,"E26.3.0.0")}),1.0]])]});
            var Q4;
            Q4=makeQuery(id+"F12.imprint","IMPRINT",FACE,{"disambiguationData":[TD([[makeQuery(id+"F12.imprint","IMPRINT",EDGE,{"derivedFrom":sQuery(id+"F12.wireOp",EDGE,"E26.4.0.0")}),1.0]])]});
            var Q5;
            Q5=makeQuery(id+"F12.imprint","IMPRINT",FACE,{"disambiguationData":[TD([[makeQuery(id+"F12.imprint","IMPRINT",EDGE,{"derivedFrom":sQuery(id+"F12.wireOp",EDGE,"E26.5.0.0")}),1.0]])]});
            var Q6;
            Q6=makeQuery(id+"F12.imprint","IMPRINT",FACE,{"disambiguationData":[TD([[makeQuery(id+"F12.imprint","IMPRINT",EDGE,{"derivedFrom":sQuery(id+"F12.wireOp",EDGE,"E26.6.0.0")}),1.0]])]});
            var Q7;
            Q7=makeQuery(id+"F12.imprint","IMPRINT",FACE,{"disambiguationData":[TD([[makeQuery(id+"F12.imprint","IMPRINT",EDGE,{"derivedFrom":sQuery(id+"F12.wireOp",EDGE,"E26.7.0.0")}),1.0]])]});
            var Q8;
            Q8=makeQuery(id+"F12.imprint","IMPRINT",FACE,{"disambiguationData":[TD([[makeQuery(id+"F12.imprint","IMPRINT",EDGE,{"derivedFrom":sQuery(id+"F12.wireOp",EDGE,"E26.8.0.0")}),1.0]])]});
            var Q9;
            Q9=makeQuery(id+"F12.imprint","IMPRINT",FACE,{"disambiguationData":[TD([[makeQuery(id+"F12.imprint","IMPRINT",EDGE,{"derivedFrom":sQuery(id+"F12.wireOp",EDGE,"E26.9.0.0")}),1.0]])]});
            var Q10;
            Q10=sQuery(id+"F12.wireOp",EDGE,"E25");
            var Q11;
            Q11=sQuery(id+"F12.wireOp",EDGE,"E26.1.0.0");
            var Q12;
            Q12=sQuery(id+"F12.wireOp",EDGE,"E26.2.0.0");
            var Q13;
            Q13=sQuery(id+"F12.wireOp",EDGE,"E26.3.0.0");
            var Q14;
            Q14=sQuery(id+"F12.wireOp",EDGE,"E26.4.0.0");
            var Q15;
            Q15=sQuery(id+"F12.wireOp",EDGE,"E26.5.0.0");
            var Q16;
            Q16=sQuery(id+"F12.wireOp",EDGE,"E26.6.0.0");
            var Q17;
            Q17=sQuery(id+"F12.wireOp",EDGE,"E26.7.0.0");
            var Q18;
            Q18=sQuery(id+"F12.wireOp",EDGE,"E26.8.0.0");
            var Q19;
            Q19=sQuery(id+"F12.wireOp",EDGE,"E26.9.0.0");
            extrude(context, id + "F13", {"entities" : qUnion([Q0, Q1, Q2, Q3, Q4, Q5, Q6, Q7, Q8, Q9]), "operationType" : NewBodyOperationType.REMOVE, "surfaceEntities" : qUnion([Q10, Q11, Q12, Q13, Q14, Q15, Q16, Q17, Q18, Q19]), "oppositeDirection" : true, "depth" : 116 * mm});
        }
        {
            var Q0;
            Q0=makeQuery(id+"F1.opExtrude","SWEPT_FACE",FACE,{"disambiguationData":[OSD([sQuery(id+"F0.wireOp",EDGE,"E9")])]});
            var sketch = newSketch(context, id + "F14", { "sketchPlane" : qUnion([Q0])});
            skCircle(sketch, "E29", {"center": v(16.13, 57.35) * mm, "radius": 12 * mm});
            skCircle(sketch, "E30.1.0.0", {"center": v(45.13, 57.35) * mm, "radius": 12 * mm});
            skCircle(sketch, "E30.2.0.0", {"center": v(74.13, 57.35) * mm, "radius": 12 * mm});
            skCircle(sketch, "E30.3.0.0", {"center": v(103.13, 57.35) * mm, "radius": 12 * mm});
            skCircle(sketch, "E30.4.0.0", {"center": v(132.13, 57.35) * mm, "radius": 12 * mm});
            skCircle(sketch, "E30.5.0.0", {"center": v(161.13, 57.35) * mm, "radius": 12 * mm});
            skCircle(sketch, "E30.6.0.0", {"center": v(190.13, 57.35) * mm, "radius": 12 * mm});
            skCircle(sketch, "E30.7.0.0", {"center": v(219.13, 57.35) * mm, "radius": 12 * mm});
            skCircle(sketch, "E30.8.0.0", {"center": v(248.13, 57.35) * mm, "radius": 12 * mm});
            skCircle(sketch, "E30.9.0.0", {"center": v(277.13, 57.35) * mm, "radius": 12 * mm});
            skLineSegment(sketch, "E30.direction1", {"start": v(16.13, 57.35) * mm, "end": v(45.13, 57.35) * mm, "construction": true});
            skCircle(sketch, "E31", {"center": v(17, 73.32) * mm, "radius": 12 * mm});
            skCircle(sketch, "E32.1.0.0", {"center": v(46, 73.32) * mm, "radius": 12 * mm});
            skCircle(sketch, "E32.2.0.0", {"center": v(75, 73.32) * mm, "radius": 12 * mm});
            skCircle(sketch, "E32.3.0.0", {"center": v(104, 73.32) * mm, "radius": 12 * mm});
            skCircle(sketch, "E32.4.0.0", {"center": v(133, 73.32) * mm, "radius": 12 * mm});
            skCircle(sketch, "E32.5.0.0", {"center": v(162, 73.32) * mm, "radius": 12 * mm});
            skCircle(sketch, "E32.6.0.0", {"center": v(191, 73.32) * mm, "radius": 12 * mm});
            skCircle(sketch, "E32.7.0.0", {"center": v(220, 73.32) * mm, "radius": 12 * mm});
            skCircle(sketch, "E32.8.0.0", {"center": v(249, 73.32) * mm, "radius": 12 * mm});
            skCircle(sketch, "E32.9.0.0", {"center": v(278, 73.32) * mm, "radius": 12 * mm});
            skLineSegment(sketch, "E32.direction1", {"start": v(17, 73.32) * mm, "end": v(46, 73.32) * mm, "construction": true});
            skSolve(sketch);
        }
        {
            var Q0;
            Q0=makeQuery(id+"F14.imprint","IMPRINT",FACE,{"disambiguationData":[TD([[makeQuery(id+"F14.imprint","IMPRINT",EDGE,{"derivedFrom":sQuery(id+"F14.wireOp",EDGE,"E29")}),1.0]])]});
            var Q1;
            Q1=makeQuery(id+"F14.imprint","IMPRINT",FACE,{"disambiguationData":[TD([[makeQuery(id+"F14.imprint","IMPRINT",EDGE,{"derivedFrom":sQuery(id+"F14.wireOp",EDGE,"E30.1.0.0")}),1.0]])]});
            var Q2;
            Q2=makeQuery(id+"F14.imprint","IMPRINT",FACE,{"disambiguationData":[TD([[makeQuery(id+"F14.imprint","IMPRINT",EDGE,{"derivedFrom":sQuery(id+"F14.wireOp",EDGE,"E30.2.0.0")}),1.0]])]});
            var Q3;
            Q3=makeQuery(id+"F14.imprint","IMPRINT",FACE,{"disambiguationData":[TD([[makeQuery(id+"F14.imprint","IMPRINT",EDGE,{"derivedFrom":sQuery(id+"F14.wireOp",EDGE,"E30.3.0.0")}),1.0]])]});
            var Q4;
            Q4=makeQuery(id+"F14.imprint","IMPRINT",FACE,{"disambiguationData":[TD([[makeQuery(id+"F14.imprint","IMPRINT",EDGE,{"derivedFrom":sQuery(id+"F14.wireOp",EDGE,"E30.4.0.0")}),1.0]])]});
            var Q5;
            Q5=makeQuery(id+"F14.imprint","IMPRINT",FACE,{"disambiguationData":[TD([[makeQuery(id+"F14.imprint","IMPRINT",EDGE,{"derivedFrom":sQuery(id+"F14.wireOp",EDGE,"E30.5.0.0")}),1.0]])]});
            var Q6;
            Q6=makeQuery(id+"F14.imprint","IMPRINT",FACE,{"disambiguationData":[TD([[makeQuery(id+"F14.imprint","IMPRINT",EDGE,{"derivedFrom":sQuery(id+"F14.wireOp",EDGE,"E30.6.0.0")}),1.0]])]});
            var Q7;
            Q7=makeQuery(id+"F14.imprint","IMPRINT",FACE,{"disambiguationData":[TD([[makeQuery(id+"F14.imprint","IMPRINT",EDGE,{"derivedFrom":sQuery(id+"F14.wireOp",EDGE,"E30.7.0.0")}),1.0]])]});
            var Q8;
            Q8=makeQuery(id+"F14.imprint","IMPRINT",FACE,{"disambiguationData":[TD([[makeQuery(id+"F14.imprint","IMPRINT",EDGE,{"derivedFrom":sQuery(id+"F14.wireOp",EDGE,"E30.8.0.0")}),1.0]])]});
            var Q9;
            Q9=makeQuery(id+"F14.imprint","IMPRINT",FACE,{"disambiguationData":[TD([[makeQuery(id+"F14.imprint","IMPRINT",EDGE,{"derivedFrom":sQuery(id+"F14.wireOp",EDGE,"E30.9.0.0")}),1.0]])]});
            var Q10;
            Q10=sQuery(id+"F14.wireOp",EDGE,"E29");
            extrude(context, id + "F15", {"entities" : qUnion([Q0, Q1, Q2, Q3, Q4, Q5, Q6, Q7, Q8, Q9]), "operationType" : NewBodyOperationType.REMOVE, "surfaceEntities" : qUnion([Q10]), "oppositeDirection" : true, "depth" : 50 * mm});
        }
        {
            var Q0;
            Q0 = qSketchRegion(id + "F14", true);
            extrude(context, id + "F16", {"entities" : qUnion([Q0]), "operationType" : NewBodyOperationType.REMOVE, "oppositeDirection" : true, "depth" : 50 * mm});
        }
        {
            var Q0;
            Q0 = qSketchRegion(id + "F12", true);
            extrude(context, id + "F17", {"entities" : qUnion([Q0]), "operationType" : NewBodyOperationType.REMOVE, "oppositeDirection" : true, "depth" : 116 * mm});
        }
        {
            var Q0;
            Q0 = qSketchRegion(id + "F10", true);
            extrude(context, id + "F18", {"entities" : qUnion([Q0]), "operationType" : NewBodyOperationType.REMOVE, "oppositeDirection" : true, "depth" : 182 * mm});
        }
    });
